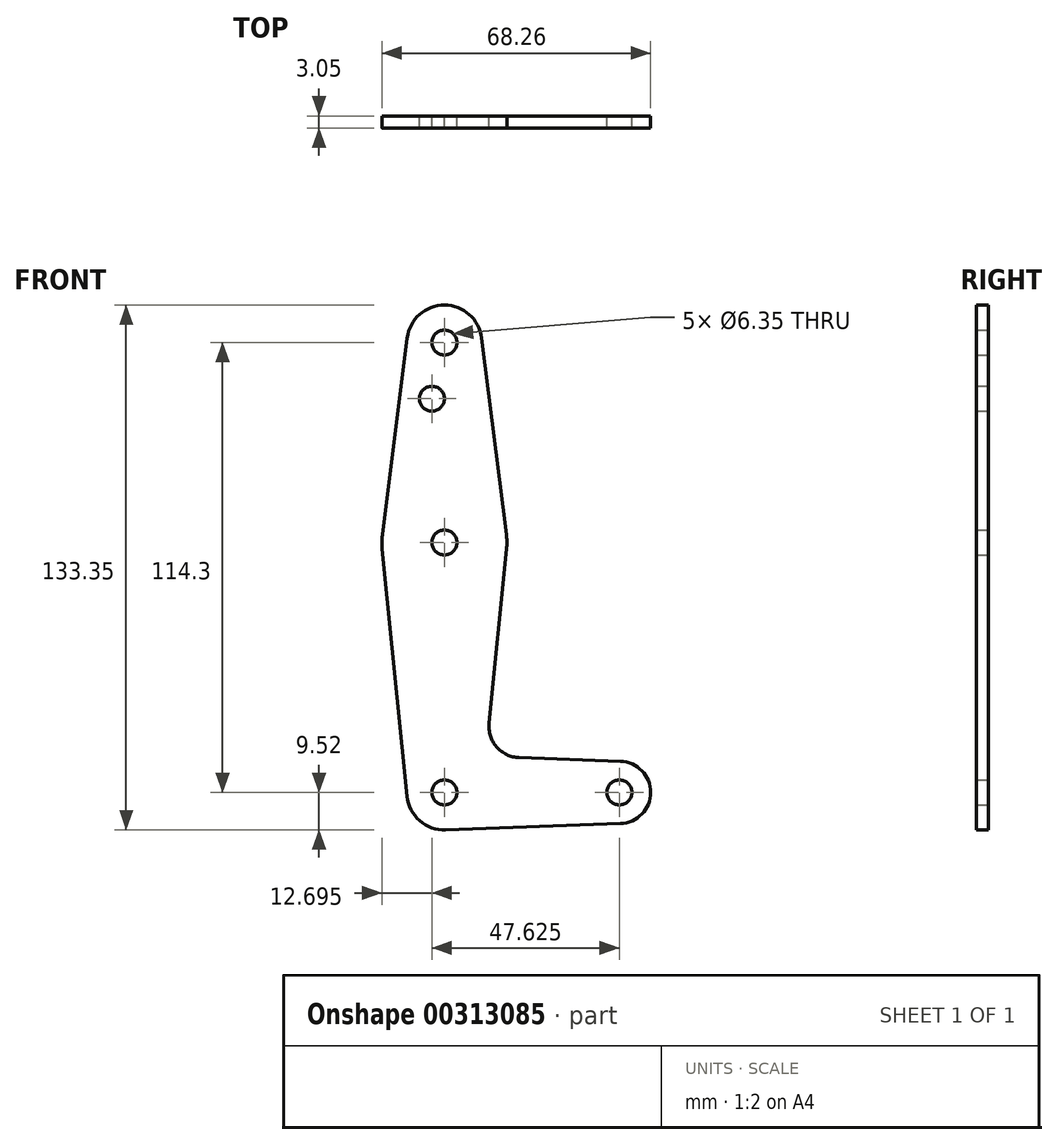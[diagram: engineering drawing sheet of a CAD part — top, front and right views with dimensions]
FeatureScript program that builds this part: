
annotation { "Feature Type Name" : "Feature", "Feature Type Description" : "" }
export const myFeature = defineFeature(function(context is Context, id is Id, definition is map)
    precondition{}
    {
        {
            var Q0;
            Q0=qCreatedBy(makeId("Front.planeOp"),FACE);
            var sketch = newSketch(context, id + "F0", { "sketchPlane" : qUnion([Q0])});
            skCircle(sketch, "E0", {"center": v(0, 114.3) * mm, "radius": 9.53 * mm});
            skCircle(sketch, "E1", {"center": v(0, 0) * mm, "radius": 9.53 * mm});
            skCircle(sketch, "E2", {"center": v(0, 63.5) * mm, "radius": 15.88 * mm});
            skCircle(sketch, "E3", {"center": v(44.45, 0) * mm, "radius": 7.94 * mm});
            skLineSegment(sketch, "E4", {"start": v(0, 114.3) * mm, "end": v(0, 0) * mm, "construction": true});
            skLineSegment(sketch, "E5", {"start": v(0, 0) * mm, "end": v(44.45, 0) * mm, "construction": true});
            skLineSegment(sketch, "E6", {"start": v(-9.45, 115.5) * mm, "end": v(-15.75, 65.48) * mm});
            skLineSegment(sketch, "E7", {"start": v(-15.8, 61.91) * mm, "end": v(-9.16, -4.11) * mm});
            skLineSegment(sketch, "E8", {"start": v(9.45, 115.5) * mm, "end": v(15.75, 65.48) * mm});
            skLineSegment(sketch, "E9", {"start": v(15.8, 61.91) * mm, "end": v(11.34, 17.6) * mm});
            skLineSegment(sketch, "E10", {"start": v(18.97, 8.85) * mm, "end": v(44.73, 7.93) * mm});
            skLineSegment(sketch, "E11", {"start": v(44.73, -7.93) * mm, "end": v(0.34, -9.52) * mm});
            skCircle(sketch, "E12", {"center": v(-3.17, 100.03) * mm, "radius": 3.18 * mm});
            skCircle(sketch, "E13", {"center": v(0, 114.3) * mm, "radius": 3.18 * mm});
            skCircle(sketch, "E14", {"center": v(0, 63.5) * mm, "radius": 3.18 * mm});
            skCircle(sketch, "E15", {"center": v(0, 0) * mm, "radius": 3.18 * mm});
            skCircle(sketch, "E16", {"center": v(44.45, 0) * mm, "radius": 3.18 * mm});
            skArc(sketch, "E17.filletArc", {"start": v(11.34, 17.6) * mm, "mid": v(13.26, 11.57) * mm, "end": v(18.97, 8.85) * mm});
            skSolve(sketch);
        }
        {
            var Q0;
            Q0 = qSketchRegion(id + "F0", true);
            extrude(context, id + "F1", {"entities" : qUnion([Q0]), "depth" : 3.05 * mm});
        }
    });
